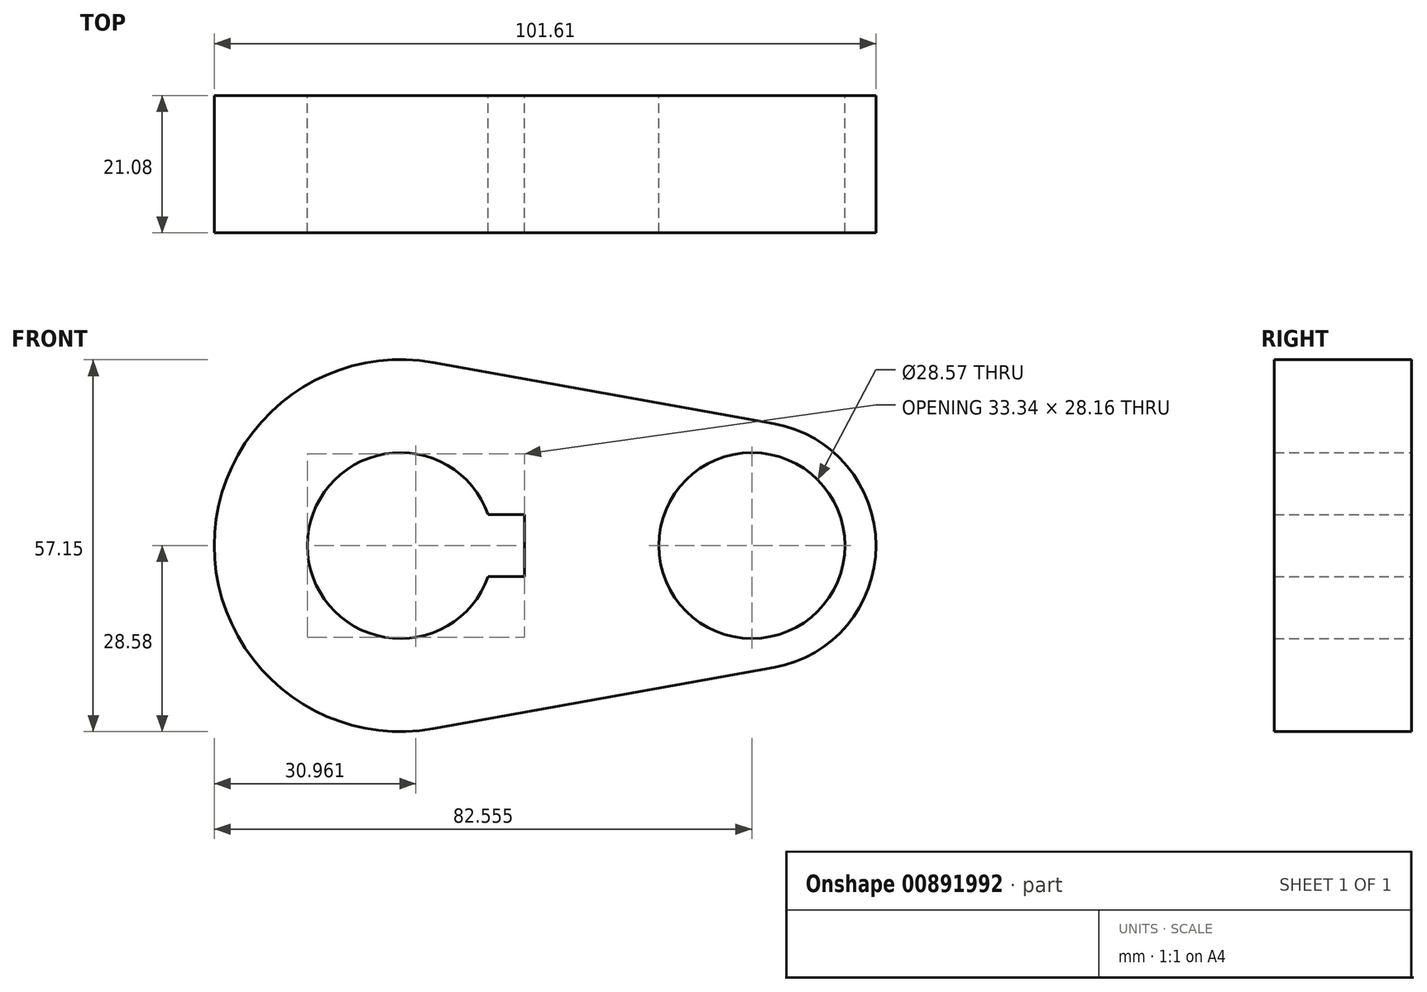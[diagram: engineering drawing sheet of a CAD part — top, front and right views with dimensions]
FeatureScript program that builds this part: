
annotation { "Feature Type Name" : "Feature", "Feature Type Description" : "" }
export const myFeature = defineFeature(function(context is Context, id is Id, definition is map)
    precondition{}
    {
        {
            var Q0;
            Q0=qCreatedBy(makeId("Front.planeOp"),FACE);
            var sketch = newSketch(context, id + "F0", { "sketchPlane" : qUnion([Q0])});
            skCircle(sketch, "E0", {"center": v(0, 0) * mm, "radius": 28.58 * mm});
            skCircle(sketch, "E1", {"center": v(53.98, 0) * mm, "radius": 19.05 * mm});
            skLineSegment(sketch, "E2", {"start": v(5.04, 28.13) * mm, "end": v(57.34, 18.75) * mm});
            skLineSegment(sketch, "E3", {"start": v(5.04, -28.13) * mm, "end": v(57.34, -18.75) * mm});
            skCircle(sketch, "E4", {"center": v(0, 0) * mm, "radius": 14.29 * mm});
            skCircle(sketch, "E5", {"center": v(53.98, 0) * mm, "radius": 14.29 * mm});
            skLineSegment(sketch, "E6.bottom", {"start": v(19.05, -4.76) * mm, "end": v(-19.05, -4.76) * mm});
            skLineSegment(sketch, "E6.top", {"start": v(19.05, 4.76) * mm, "end": v(-19.05, 4.76) * mm});
            skLineSegment(sketch, "E6.left", {"start": v(19.05, -4.76) * mm, "end": v(19.05, 4.76) * mm});
            skLineSegment(sketch, "E6.right", {"start": v(-19.05, -4.76) * mm, "end": v(-19.05, 4.76) * mm});
            skSolve(sketch);
        }
        {
            var Q0;
            {var subQ7=sQuery(id+"F0.wireOp",EDGE,"E6.left");Q0=makeQuery(id+"F0.imprint","IMPRINT",FACE,{"disambiguationData":[TD([[makeQuery(id+"F0.imprint","IMPRINT",EDGE,{"derivedFrom":subQ7}),-1.0]])]});}
            var Q1;
            {var subQ0=sQuery(id+"F0.wireOp",EDGE,"E2");Q1=makeQuery(id+"F0.imprint","IMPRINT",FACE,{"disambiguationData":[TD([[makeQuery(id+"F0.imprint","IMPRINT",EDGE,{"derivedFrom":subQ0}),-1.0]])]});}
            var Q2;
            Q2=makeQuery(id+"F0.imprint","IMPRINT",FACE,{"disambiguationData":[TD([[makeQuery(id+"F0.imprint","IMPRINT",EDGE,{"derivedFrom":sQuery(id+"F0.wireOp",EDGE,"E5")}),-1.0]])]});
            var Q3;
            {var subQ5=sQuery(id+"F0.wireOp",EDGE,"E6.right");Q3=makeQuery(id+"F0.imprint","IMPRINT",FACE,{"disambiguationData":[TD([[makeQuery(id+"F0.imprint","IMPRINT",EDGE,{"derivedFrom":subQ5}),-1.0]])]});}
            extrude(context, id + "F1", {"entities" : qUnion([Q0, Q1, Q2, Q3]), "depth" : 21.08 * mm, "offsetDistance" : 25.4 * mm});
        }
    });
